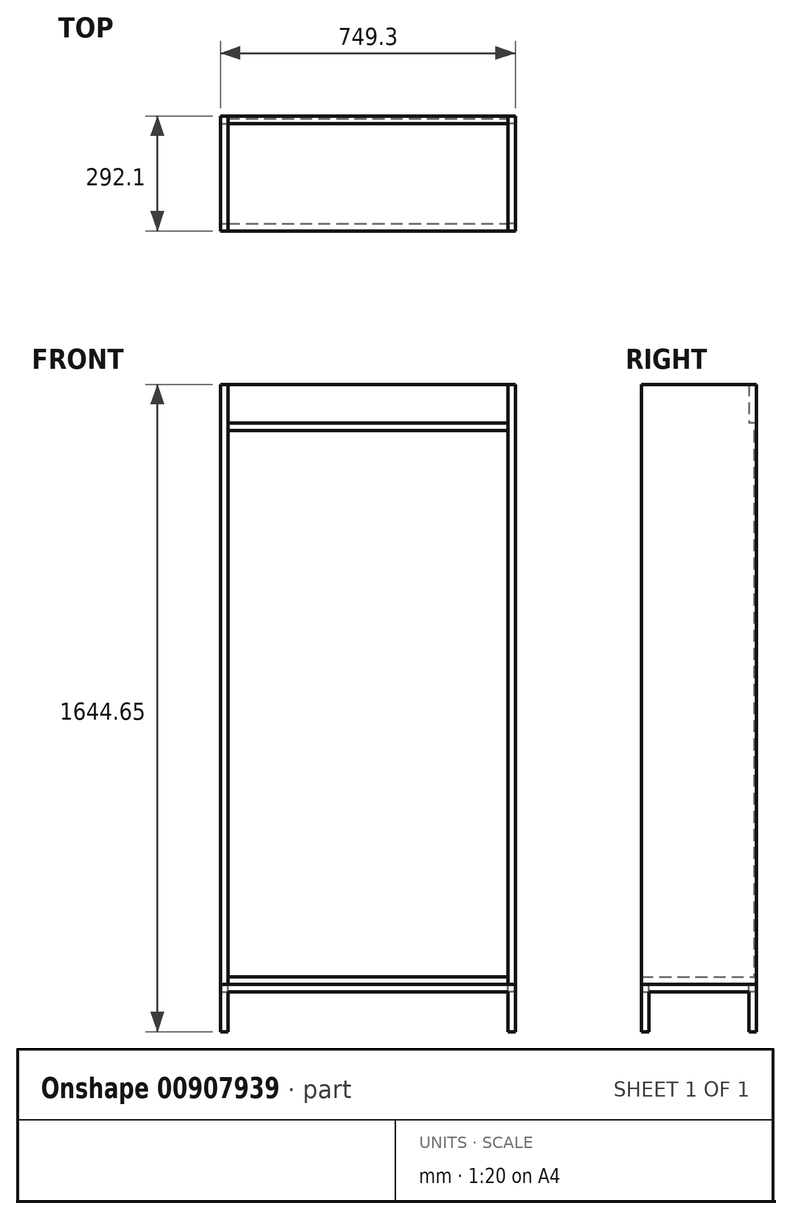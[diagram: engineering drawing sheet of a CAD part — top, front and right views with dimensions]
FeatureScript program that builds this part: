
annotation { "Feature Type Name" : "Feature", "Feature Type Description" : "" }
export const myFeature = defineFeature(function(context is Context, id is Id, definition is map)
    precondition{}
    {
        {
            var Q0;
            Q0=qCreatedBy(makeId("Front.planeOp"),FACE);
            var sketch = newSketch(context, id + "F0", { "sketchPlane" : qUnion([Q0])});
            skLineSegment(sketch, "E0.top", {"start": v(-355.6, -762) * mm, "end": v(355.6, -762) * mm});
            skLineSegment(sketch, "E0.left", {"start": v(-355.6, 762) * mm, "end": v(-355.6, -762) * mm});
            skLineSegment(sketch, "E0.right", {"start": v(355.6, 762) * mm, "end": v(355.6, -762) * mm});
            skPoint(sketch, "E0.middle", {"position": v(0, 0) * mm});
            skLineSegment(sketch, "E1", {"start": v(355.6, -762) * mm, "end": v(0, -762) * mm});
            skLineSegment(sketch, "E2", {"start": v(177.8, 762) * mm, "end": v(0, -762) * mm});
            skLineSegment(sketch, "E3", {"start": v(355.6, -406.4) * mm, "end": v(41.49, -406.4) * mm});
            skLineSegment(sketch, "E4", {"start": v(355.6, -92.29) * mm, "end": v(78.13, -92.29) * mm});
            skLineSegment(sketch, "E5", {"start": v(355.6, 185.18) * mm, "end": v(110.5, 185.18) * mm});
            skLineSegment(sketch, "E6", {"start": v(355.6, 430.28) * mm, "end": v(139.1, 430.28) * mm});
            skLineSegment(sketch, "E7", {"start": v(355.6, 644.24) * mm, "end": v(164.06, 644.24) * mm});
            skLineSegment(sketch, "E8.bottom", {"start": v(355.6, 644.24) * mm, "end": v(-355.6, 644.24) * mm});
            skLineSegment(sketch, "E8.top", {"start": v(355.6, 625.19) * mm, "end": v(-355.6, 625.19) * mm});
            skLineSegment(sketch, "E8.left", {"start": v(355.6, 644.24) * mm, "end": v(355.6, 625.19) * mm});
            skLineSegment(sketch, "E8.right", {"start": v(-355.6, 644.24) * mm, "end": v(-355.6, 625.19) * mm});
            skLineSegment(sketch, "E9.bottom", {"start": v(355.6, 430.28) * mm, "end": v(-355.6, 430.28) * mm});
            skLineSegment(sketch, "E9.top", {"start": v(355.6, 411.23) * mm, "end": v(-355.6, 411.23) * mm});
            skLineSegment(sketch, "E9.left", {"start": v(355.6, 430.28) * mm, "end": v(355.6, 411.23) * mm});
            skLineSegment(sketch, "E9.right", {"start": v(-355.6, 430.28) * mm, "end": v(-355.6, 411.23) * mm});
            skLineSegment(sketch, "E10.bottom", {"start": v(355.6, 185.18) * mm, "end": v(-355.6, 185.18) * mm});
            skLineSegment(sketch, "E10.top", {"start": v(355.6, 166.13) * mm, "end": v(-355.6, 166.13) * mm});
            skLineSegment(sketch, "E10.left", {"start": v(355.6, 185.18) * mm, "end": v(355.6, 166.13) * mm});
            skLineSegment(sketch, "E10.right", {"start": v(-355.6, 185.18) * mm, "end": v(-355.6, 166.13) * mm});
            skLineSegment(sketch, "E11.bottom", {"start": v(355.6, -92.29) * mm, "end": v(-355.6, -92.29) * mm});
            skLineSegment(sketch, "E11.top", {"start": v(355.6, -111.34) * mm, "end": v(-355.6, -111.34) * mm});
            skLineSegment(sketch, "E11.left", {"start": v(355.6, -92.29) * mm, "end": v(355.6, -111.34) * mm});
            skLineSegment(sketch, "E11.right", {"start": v(-355.6, -92.29) * mm, "end": v(-355.6, -111.34) * mm});
            skLineSegment(sketch, "E12.bottom", {"start": v(355.6, -406.4) * mm, "end": v(-355.6, -406.4) * mm});
            skLineSegment(sketch, "E12.top", {"start": v(355.6, -425.45) * mm, "end": v(-355.6, -425.45) * mm});
            skLineSegment(sketch, "E12.left", {"start": v(355.6, -406.4) * mm, "end": v(355.6, -425.45) * mm});
            skLineSegment(sketch, "E12.right", {"start": v(-355.6, -406.4) * mm, "end": v(-355.6, -425.45) * mm});
            skLineSegment(sketch, "E13.bottom", {"start": v(355.6, -762) * mm, "end": v(-355.6, -762) * mm});
            skLineSegment(sketch, "E13.top", {"start": v(355.6, -781.05) * mm, "end": v(-355.6, -781.05) * mm});
            skLineSegment(sketch, "E13.left", {"start": v(355.6, -762) * mm, "end": v(355.6, -781.05) * mm});
            skLineSegment(sketch, "E13.right", {"start": v(-355.6, -762) * mm, "end": v(-355.6, -781.05) * mm});
            skLineSegment(sketch, "E14.top", {"start": v(355.6, 742.95) * mm, "end": v(-355.6, 742.95) * mm});
            skLineSegment(sketch, "E14.left", {"start": v(355.6, 762) * mm, "end": v(355.6, 742.95) * mm});
            skLineSegment(sketch, "E14.right", {"start": v(-355.6, 762) * mm, "end": v(-355.6, 742.95) * mm});
            skSolve(sketch);
        }
        {
            var Q0;
            Q0=makeQuery(id+"F0.imprint","IMPRINT",FACE,{"disambiguationData":[TD([[makeQuery(id+"F0.imprint","IMPRINT",EDGE,{"derivedFrom":sQuery(id+"F0.wireOp",EDGE,"E13.top")}),-1.0]])]});
            var Q1;
            {var subQ5=sQuery(id+"F0.wireOp",EDGE,"E8.left");Q1=makeQuery(id+"F0.imprint","IMPRINT",FACE,{"disambiguationData":[TD([[makeQuery(id+"F0.imprint","IMPRINT",EDGE,{"derivedFrom":subQ5}),-1.0]])]});}
            var Q2;
            {var subQ5=sQuery(id+"F0.wireOp",EDGE,"E9.left");Q2=makeQuery(id+"F0.imprint","IMPRINT",FACE,{"disambiguationData":[TD([[makeQuery(id+"F0.imprint","IMPRINT",EDGE,{"derivedFrom":subQ5}),-1.0]])]});}
            var Q3;
            {var subQ5=sQuery(id+"F0.wireOp",EDGE,"E9.right");Q3=makeQuery(id+"F0.imprint","IMPRINT",FACE,{"disambiguationData":[TD([[makeQuery(id+"F0.imprint","IMPRINT",EDGE,{"derivedFrom":subQ5}),1.0]])]});}
            var Q4;
            {var subQ5=sQuery(id+"F0.wireOp",EDGE,"E10.left");Q4=makeQuery(id+"F0.imprint","IMPRINT",FACE,{"disambiguationData":[TD([[makeQuery(id+"F0.imprint","IMPRINT",EDGE,{"derivedFrom":subQ5}),-1.0]])]});}
            var Q5;
            {var subQ5=sQuery(id+"F0.wireOp",EDGE,"E10.right");Q5=makeQuery(id+"F0.imprint","IMPRINT",FACE,{"disambiguationData":[TD([[makeQuery(id+"F0.imprint","IMPRINT",EDGE,{"derivedFrom":subQ5}),1.0]])]});}
            var Q6;
            {var subQ5=sQuery(id+"F0.wireOp",EDGE,"E11.left");Q6=makeQuery(id+"F0.imprint","IMPRINT",FACE,{"disambiguationData":[TD([[makeQuery(id+"F0.imprint","IMPRINT",EDGE,{"derivedFrom":subQ5}),-1.0]])]});}
            var Q7;
            {var subQ5=sQuery(id+"F0.wireOp",EDGE,"E11.right");Q7=makeQuery(id+"F0.imprint","IMPRINT",FACE,{"disambiguationData":[TD([[makeQuery(id+"F0.imprint","IMPRINT",EDGE,{"derivedFrom":subQ5}),1.0]])]});}
            var Q8;
            {var subQ5=sQuery(id+"F0.wireOp",EDGE,"E12.left");Q8=makeQuery(id+"F0.imprint","IMPRINT",FACE,{"disambiguationData":[TD([[makeQuery(id+"F0.imprint","IMPRINT",EDGE,{"derivedFrom":subQ5}),-1.0]])]});}
            var Q9;
            {var subQ5=sQuery(id+"F0.wireOp",EDGE,"E12.right");Q9=makeQuery(id+"F0.imprint","IMPRINT",FACE,{"disambiguationData":[TD([[makeQuery(id+"F0.imprint","IMPRINT",EDGE,{"derivedFrom":subQ5}),1.0]])]});}
            var Q10;
            {var subQ5=sQuery(id+"F0.wireOp",EDGE,"E8.right");Q10=makeQuery(id+"F0.imprint","IMPRINT",FACE,{"disambiguationData":[TD([[makeQuery(id+"F0.imprint","IMPRINT",EDGE,{"derivedFrom":subQ5}),1.0]])]});}
            extrude(context, id + "F1", {"entities" : qUnion([Q0, Q1, Q2, Q3, Q4, Q5, Q6, Q7, Q8, Q9, Q10]), "depth" : 292.1 * mm, "offsetDistance" : 25.4 * mm});
        }
        {
            var Q0;
            Q0=qCreatedBy(makeId("Front.planeOp"),FACE);
            var sketch = newSketch(context, id + "F2", { "sketchPlane" : qUnion([Q0])});
            skPoint(sketch, "E15.0", {"position": v(355.6, -781.05) * mm});
            skPoint(sketch, "E16.0", {"position": v(-355.6, -781.05) * mm});
            skLineSegment(sketch, "E17.bottom", {"start": v(355.6, -781.05) * mm, "end": v(374.65, -781.05) * mm});
            skLineSegment(sketch, "E17.top", {"start": v(355.6, 742.95) * mm, "end": v(374.65, 742.95) * mm});
            skLineSegment(sketch, "E17.left", {"start": v(355.6, -781.05) * mm, "end": v(355.6, 742.95) * mm});
            skLineSegment(sketch, "E17.right", {"start": v(374.65, -781.05) * mm, "end": v(374.65, 742.95) * mm});
            skLineSegment(sketch, "E18.bottom", {"start": v(-355.6, -781.05) * mm, "end": v(-374.65, -781.05) * mm});
            skLineSegment(sketch, "E18.top", {"start": v(-355.6, 742.95) * mm, "end": v(-374.65, 742.95) * mm});
            skLineSegment(sketch, "E18.left", {"start": v(-355.6, -781.05) * mm, "end": v(-355.6, 742.95) * mm});
            skLineSegment(sketch, "E18.right", {"start": v(-374.65, -781.05) * mm, "end": v(-374.65, 742.95) * mm});
            skSolve(sketch);
        }
        {
            var Q0;
            Q0=makeQuery(id+"F2.imprint","IMPRINT",FACE,{"disambiguationData":[TD([[makeQuery(id+"F2.imprint","IMPRINT",EDGE,{"derivedFrom":sQuery(id+"F2.wireOp",EDGE,"E18.bottom")}),-1.0]])]});
            var Q1;
            Q1=makeQuery(id+"F2.imprint","IMPRINT",FACE,{"disambiguationData":[TD([[makeQuery(id+"F2.imprint","IMPRINT",EDGE,{"derivedFrom":sQuery(id+"F2.wireOp",EDGE,"E17.bottom")}),1.0]])]});
            extrude(context, id + "F3", {"entities" : qUnion([Q0, Q1]), "depth" : 292.1 * mm, "offsetDistance" : 25.4 * mm});
        }
        {
            var Q0;
            Q0=makeQuery(id+"F3.opExtrude","SWEPT_FACE",FACE,{"disambiguationData":[OSD([sQuery(id+"F2.wireOp",EDGE,"E18.left")])]});
            var sketch = newSketch(context, id + "F4", { "sketchPlane" : qUnion([Q0])});
            skPoint(sketch, "E19.0", {"position": v(0, 644.24) * mm});
            skLineSegment(sketch, "E20.bottom", {"start": v(0, 742.95) * mm, "end": v(-19.05, 742.95) * mm});
            skLineSegment(sketch, "E20.top", {"start": v(0, 644.24) * mm, "end": v(-19.05, 644.24) * mm});
            skLineSegment(sketch, "E20.left", {"start": v(0, 742.95) * mm, "end": v(0, 644.24) * mm});
            skLineSegment(sketch, "E20.right", {"start": v(-19.05, 742.95) * mm, "end": v(-19.05, 644.24) * mm});
            skSolve(sketch);
        }
        {
            var Q0;
            Q0 = qSketchRegion(id + "F4", true);
            extrude(context, id + "F5", {"entities" : qUnion([Q0]), "depth" : 711.2 * mm, "offsetDistance" : 25.4 * mm});
        }
        {
            var Q0;
            Q0=makeQuery(id+"F1.opExtrude","SWEPT_FACE",FACE,{"disambiguationData":[OSD([sQuery(id+"F0.wireOp",EDGE,"E13.top")])]});
            var sketch = newSketch(context, id + "F6", { "sketchPlane" : qUnion([Q0])});
            skPoint(sketch, "E21.0", {"position": v(-374.65, 292.1) * mm});
            skPoint(sketch, "E22.0", {"position": v(374.65, 0) * mm});
            skLineSegment(sketch, "E23.bottom", {"start": v(-374.65, 292.1) * mm, "end": v(374.65, 292.1) * mm});
            skLineSegment(sketch, "E23.top", {"start": v(-374.65, 0) * mm, "end": v(374.65, 0) * mm});
            skLineSegment(sketch, "E23.left", {"start": v(-374.65, 292.1) * mm, "end": v(-374.65, 0) * mm});
            skLineSegment(sketch, "E23.right", {"start": v(374.65, 292.1) * mm, "end": v(374.65, 0) * mm});
            skLineSegment(sketch, "E24.0", {"start": v(-355.6, 273.05) * mm, "end": v(355.6, 273.05) * mm});
            skLineSegment(sketch, "E24.1", {"start": v(-355.6, 273.05) * mm, "end": v(-355.6, 19.05) * mm});
            skLineSegment(sketch, "E24.2", {"start": v(-355.6, 19.05) * mm, "end": v(355.6, 19.05) * mm});
            skLineSegment(sketch, "E24.3", {"start": v(355.6, 273.05) * mm, "end": v(355.6, 19.05) * mm});
            skSolve(sketch);
        }
        {
            var Q0;
            {var subQ6=sQuery(id+"F6.wireOp",EDGE,"E24.0");Q0=makeQuery(id+"F6.imprint","IMPRINT",FACE,{"disambiguationData":[TD([[makeQuery(id+"F6.imprint","IMPRINT",EDGE,{"derivedFrom":subQ6}),1.0]])]});}
            var Q1;
            {var subQ1=sQuery(id+"F6.wireOp",EDGE,"E23.left");Q1=makeQuery(id+"F6.imprint","IMPRINT",FACE,{"disambiguationData":[TD([[makeQuery(id+"F6.imprint","IMPRINT",EDGE,{"derivedFrom":subQ1}),1.0]])]});}
            var Q2;
            {var subQ6=sQuery(id+"F6.wireOp",EDGE,"E24.2");Q2=makeQuery(id+"F6.imprint","IMPRINT",FACE,{"disambiguationData":[TD([[makeQuery(id+"F6.imprint","IMPRINT",EDGE,{"derivedFrom":subQ6}),-1.0]])]});}
            var Q3;
            {var subQ4=sQuery(id+"F6.wireOp",EDGE,"E23.right");Q3=makeQuery(id+"F6.imprint","IMPRINT",FACE,{"disambiguationData":[TD([[makeQuery(id+"F6.imprint","IMPRINT",EDGE,{"derivedFrom":subQ4}),-1.0]])]});}
            extrude(context, id + "F7", {"entities" : qUnion([Q0, Q1, Q2, Q3]), "depth" : 19.05 * mm, "offsetDistance" : 25.4 * mm});
        }
        {
            var Q0;
            Q0=makeQuery(id+"F7.opExtrude","CAP_FACE",FACE,{"disambiguationData":[OSD([sQuery(id+"F6.wireOp",EDGE,"E23.bottom"),sQuery(id+"F6.wireOp",EDGE,"E23.top"),sQuery(id+"F6.wireOp",EDGE,"E23.left"),sQuery(id+"F6.wireOp",EDGE,"E23.right"),sQuery(id+"F6.wireOp",EDGE,"E24.0"),sQuery(id+"F6.wireOp",EDGE,"E24.1"),sQuery(id+"F6.wireOp",EDGE,"E24.2"),sQuery(id+"F6.wireOp",EDGE,"E24.3")])],"isStart":false});
            var sketch = newSketch(context, id + "F8", { "sketchPlane" : qUnion([Q0])});
            skLineSegment(sketch, "E25.bottom", {"start": v(-374.65, 292.1) * mm, "end": v(-355.6, 292.1) * mm});
            skLineSegment(sketch, "E25.top", {"start": v(-374.65, 273.05) * mm, "end": v(-355.6, 273.05) * mm});
            skLineSegment(sketch, "E25.left", {"start": v(-374.65, 292.1) * mm, "end": v(-374.65, 273.05) * mm});
            skLineSegment(sketch, "E25.right", {"start": v(-355.6, 292.1) * mm, "end": v(-355.6, 273.05) * mm});
            skLineSegment(sketch, "E26.bottom", {"start": v(374.65, 292.1) * mm, "end": v(355.6, 292.1) * mm});
            skLineSegment(sketch, "E26.top", {"start": v(374.65, 273.05) * mm, "end": v(355.6, 273.05) * mm});
            skLineSegment(sketch, "E26.left", {"start": v(374.65, 292.1) * mm, "end": v(374.65, 273.05) * mm});
            skLineSegment(sketch, "E26.right", {"start": v(355.6, 292.1) * mm, "end": v(355.6, 273.05) * mm});
            skLineSegment(sketch, "E27.bottom", {"start": v(374.65, 0) * mm, "end": v(355.6, 0) * mm});
            skLineSegment(sketch, "E27.top", {"start": v(374.65, 19.05) * mm, "end": v(355.6, 19.05) * mm});
            skLineSegment(sketch, "E27.left", {"start": v(374.65, 0) * mm, "end": v(374.65, 19.05) * mm});
            skLineSegment(sketch, "E27.right", {"start": v(355.6, 0) * mm, "end": v(355.6, 19.05) * mm});
            skLineSegment(sketch, "E28.bottom", {"start": v(-374.65, 0) * mm, "end": v(-355.6, 0) * mm});
            skLineSegment(sketch, "E28.top", {"start": v(-374.65, 19.05) * mm, "end": v(-355.6, 19.05) * mm});
            skLineSegment(sketch, "E28.left", {"start": v(-374.65, 0) * mm, "end": v(-374.65, 19.05) * mm});
            skLineSegment(sketch, "E28.right", {"start": v(-355.6, 0) * mm, "end": v(-355.6, 19.05) * mm});
            skSolve(sketch);
        }
        {
            var Q0;
            Q0=makeQuery(id+"F8.imprint","IMPRINT",FACE,{"disambiguationData":[TD([[makeQuery(id+"F8.imprint","IMPRINT",EDGE,{"derivedFrom":sQuery(id+"F8.wireOp",EDGE,"E25.bottom")}),1.0]])]});
            var Q1;
            Q1=makeQuery(id+"F8.imprint","IMPRINT",FACE,{"disambiguationData":[TD([[makeQuery(id+"F8.imprint","IMPRINT",EDGE,{"derivedFrom":sQuery(id+"F8.wireOp",EDGE,"E28.bottom")}),1.0]])]});
            var Q2;
            Q2=makeQuery(id+"F8.imprint","IMPRINT",FACE,{"disambiguationData":[TD([[makeQuery(id+"F8.imprint","IMPRINT",EDGE,{"derivedFrom":sQuery(id+"F8.wireOp",EDGE,"E27.bottom")}),1.0]])]});
            var Q3;
            Q3=makeQuery(id+"F8.imprint","IMPRINT",FACE,{"disambiguationData":[TD([[makeQuery(id+"F8.imprint","IMPRINT",EDGE,{"derivedFrom":sQuery(id+"F8.wireOp",EDGE,"E26.bottom")}),1.0]])]});
            extrude(context, id + "F9", {"entities" : qUnion([Q0, Q1, Q2, Q3]), "operationType" : NewBodyOperationType.ADD, "depth" : 101.6 * mm, "offsetDistance" : 25.4 * mm});
        }
        {
            var Q0;
            Q0=qCreatedBy(makeId("Front.planeOp"),FACE);
            var sketch = newSketch(context, id + "F10", { "sketchPlane" : qUnion([Q0])});
            skPoint(sketch, "E29.0", {"position": v(-355.6, 625.19) * mm});
            skPoint(sketch, "E30.0", {"position": v(355.6, -762) * mm});
            skLineSegment(sketch, "E31.bottom", {"start": v(-355.6, 625.19) * mm, "end": v(355.6, 625.19) * mm});
            skLineSegment(sketch, "E31.top", {"start": v(-355.6, -762) * mm, "end": v(355.6, -762) * mm});
            skLineSegment(sketch, "E31.left", {"start": v(-355.6, 625.19) * mm, "end": v(-355.6, -762) * mm});
            skLineSegment(sketch, "E31.right", {"start": v(355.6, 625.19) * mm, "end": v(355.6, -762) * mm});
            skSolve(sketch);
        }
        {
            var Q0;
            Q0 = qSketchRegion(id + "F10", true);
            extrude(context, id + "F11", {"entities" : qUnion([Q0]), "depth" : 6.35 * mm, "offsetDistance" : 25.4 * mm});
        }
    });
